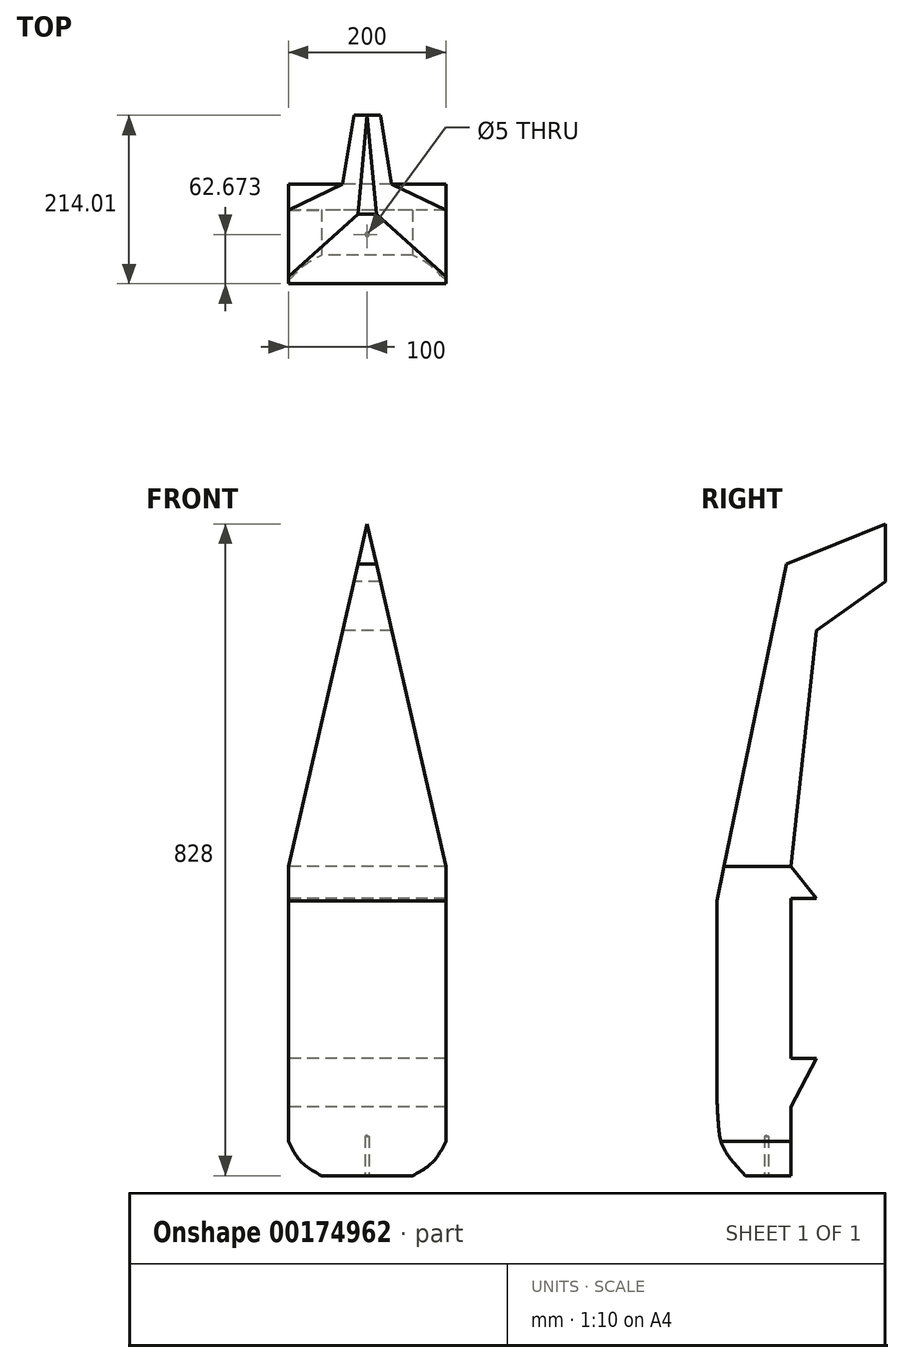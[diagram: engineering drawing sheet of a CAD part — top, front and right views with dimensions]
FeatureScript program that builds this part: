
annotation { "Feature Type Name" : "Feature", "Feature Type Description" : "" }
export const myFeature = defineFeature(function(context is Context, id is Id, definition is map)
    precondition{}
    {
        {
            var Q0;
            Q0=qCreatedBy(makeId("Top.planeOp"),FACE);
            var sketch = newSketch(context, id + "F0", { "sketchPlane" : qUnion([Q0])});
            skLineSegment(sketch, "E0.bottom", {"start": v(-100, 136) * mm, "end": v(100, 136) * mm});
            skLineSegment(sketch, "E0.top", {"start": v(-100, -136) * mm, "end": v(100, -136) * mm});
            skLineSegment(sketch, "E0.left", {"start": v(100, 136) * mm, "end": v(100, -136) * mm});
            skLineSegment(sketch, "E0.right", {"start": v(-100, 136) * mm, "end": v(-100, -136) * mm});
            skSolve(sketch);
        }
        {
            var Q0;
            Q0 = qSketchRegion(id + "F0", true);
            extrude(context, id + "F1", {"entities" : qUnion([Q0]), "endBound" : BoundingType.SYMMETRIC, "depth" : 828 * mm});
        }
        {
            var Q0;
            Q0=makeQuery(id+"F1.opExtrude","SWEPT_FACE",FACE,{"disambiguationData":[OSD([sQuery(id+"F0.wireOp",EDGE,"E0.right")])]});
            var sketch = newSketch(context, id + "F2", { "sketchPlane" : qUnion([Q0])});
            skLineSegment(sketch, "E1", {"start": v(-136, 414) * mm, "end": v(-136, 340.75) * mm});
            skLineSegment(sketch, "E2", {"start": v(-136, 340.75) * mm, "end": v(-48.64, 278.29) * mm});
            skLineSegment(sketch, "E3", {"start": v(-48.64, 278.29) * mm, "end": v(-15.68, -21.04) * mm});
            skLineSegment(sketch, "E4", {"start": v(-15.68, -21.04) * mm, "end": v(-48.64, -61.76) * mm});
            skLineSegment(sketch, "E5", {"start": v(-48.64, -61.76) * mm, "end": v(-15.68, -61.76) * mm});
            skLineSegment(sketch, "E6", {"start": v(-15.68, -61.76) * mm, "end": v(-15.68, -264.75) * mm});
            skLineSegment(sketch, "E7", {"start": v(-15.68, -264.75) * mm, "end": v(-48.64, -264.75) * mm});
            skLineSegment(sketch, "E8", {"start": v(-48.64, -264.75) * mm, "end": v(-15.68, -326.7) * mm});
            skPoint(sketch, "E8.endSnap0", {"position": v(-15.68, -163.26) * mm});
            skLineSegment(sketch, "E9", {"start": v(-15.68, -326.7) * mm, "end": v(-15.68, -414) * mm});
            skLineSegment(sketch, "E10", {"start": v(-15.68, -414) * mm, "end": v(41.58, -414) * mm});
            skFitSpline(sketch, "E11", {"points": [v(41.58, -414) * mm, v(69.34, -379.26) * mm, v(76.28, -348.03) * mm, v(78.01, -301.19) * mm], "startDerivative": vector(94.66, 99.8) * mm, "endDerivative": vector(0, 138.12) * mm});
            skLineSegment(sketch, "E12", {"start": v(78.01, -301.19) * mm, "end": v(78.01, -65.23) * mm});
            skLineSegment(sketch, "E13", {"start": v(78.01, -65.23) * mm, "end": v(-10.47, 363.3) * mm});
            skLineSegment(sketch, "E14", {"start": v(-10.47, 363.3) * mm, "end": v(-136, 414) * mm});
            skLineSegment(sketch, "E15.0", {"start": v(-136, 414) * mm, "end": v(-136, -414) * mm});
            skLineSegment(sketch, "E16.0", {"start": v(136, 414) * mm, "end": v(136, -414) * mm});
            skLineSegment(sketch, "E17.0", {"start": v(-136, 414) * mm, "end": v(136, 414) * mm});
            skLineSegment(sketch, "E18.0", {"start": v(-136, -414) * mm, "end": v(136, -414) * mm});
            skSolve(sketch);
        }
        {
            var Q0;
            {var subQ0=sQuery(id+"F2.wireOp",EDGE,"E2");Q0=makeQuery(id+"F2.imprint","IMPRINT",FACE,{"disambiguationData":[TD([[makeQuery(id+"F2.imprint","IMPRINT",EDGE,{"derivedFrom":subQ0}),-1.0]])]});}
            var Q1;
            {var subQ0=sQuery(id+"F2.wireOp",EDGE,"E11");Q1=makeQuery(id+"F2.imprint","IMPRINT",FACE,{"disambiguationData":[TD([[makeQuery(id+"F2.imprint","IMPRINT",EDGE,{"derivedFrom":subQ0}),-1.0]])]});}
            extrude(context, id + "F3", {"entities" : qUnion([Q0, Q1]), "operationType" : NewBodyOperationType.REMOVE, "endBound" : BoundingType.THROUGH_ALL, "oppositeDirection" : true, "depth" : 25 * mm});
        }
        {
            var Q0;
            Q0=makeQuery(id+"F3.boolean.opBoolean","COPY",FACE,{"derivedFrom":makeQuery(id+"F3.opExtrude","SWEPT_FACE",FACE,{"disambiguationData":[OSD([sQuery(id+"F2.wireOp",EDGE,"E12")])]})});
            var sketch = newSketch(context, id + "F4", { "sketchPlane" : qUnion([Q0])});
            skPoint(sketch, "E19.0", {"position": v(0, 414) * mm});
            skPoint(sketch, "E20.0", {"position": v(100, -21.04) * mm});
            skPoint(sketch, "E21.0", {"position": v(-100, -21.04) * mm});
            skPoint(sketch, "E22.0", {"position": v(100, -326.7) * mm});
            skPoint(sketch, "E23.0", {"position": v(100, -370.35) * mm});
            skPoint(sketch, "E24.0", {"position": v(100, -414) * mm});
            skLineSegment(sketch, "E25.0", {"start": v(100, -414) * mm, "end": v(-100, -414) * mm});
            skLineSegment(sketch, "E26.0.1", {"start": v(-100, -414) * mm, "end": v(-100, -326.7) * mm});
            skLineSegment(sketch, "E26.0.2", {"start": v(-100, -326.7) * mm, "end": v(100, -326.7) * mm});
            skLineSegment(sketch, "E26.0.3", {"start": v(100, -326.7) * mm, "end": v(100, -414) * mm});
            skLineSegment(sketch, "E27", {"start": v(0, 414) * mm, "end": v(100, -21.04) * mm});
            skLineSegment(sketch, "E28", {"start": v(-100, -21.04) * mm, "end": v(0, 414) * mm});
            skLineSegment(sketch, "E29", {"start": v(-100, -21.04) * mm, "end": v(100, -21.04) * mm});
            skFitSpline(sketch, "E30", {"points": [v(100, -370.35) * mm, v(84.02, -396.08) * mm, v(57.93, -414) * mm], "startDerivative": vector(-27.55, -56.15) * mm, "endDerivative": vector(-56.5, -31.25) * mm});
            skFitSpline(sketch, "E31.MirrorCS", {"points": [v(-100, -370.35) * mm, v(-84.02, -396.08) * mm, v(-57.93, -414) * mm], "startDerivative": vector(27.55, -56.15) * mm, "endDerivative": vector(56.5, -31.25) * mm});
            skLineSegment(sketch, "E32.0", {"start": v(100, -21.04) * mm, "end": v(100, 278.29) * mm});
            skLineSegment(sketch, "E33.0", {"start": v(100, 278.29) * mm, "end": v(100, 340.75) * mm});
            skLineSegment(sketch, "E34.0", {"start": v(100, 414) * mm, "end": v(100, 340.75) * mm});
            skLineSegment(sketch, "E35.0", {"start": v(-100, 414) * mm, "end": v(100, 414) * mm});
            skLineSegment(sketch, "E36.0", {"start": v(-100, 414) * mm, "end": v(-100, 340.75) * mm});
            skLineSegment(sketch, "E37.0", {"start": v(-100, 340.75) * mm, "end": v(-100, 278.29) * mm});
            skLineSegment(sketch, "E38.0", {"start": v(-100, 278.29) * mm, "end": v(-100, -21.04) * mm});
            skSolve(sketch);
        }
        {
            var Q0;
            {var subQ2=sQuery(id+"F4.wireOp",EDGE,"E28");Q0=makeQuery(id+"F4.imprint","IMPRINT",FACE,{"disambiguationData":[TD([[makeQuery(id+"F4.imprint","IMPRINT",EDGE,{"derivedFrom":subQ2}),1.0]])]});}
            var Q1;
            {var subQ1=sQuery(id+"F4.wireOp",EDGE,"E27");Q1=makeQuery(id+"F4.imprint","IMPRINT",FACE,{"disambiguationData":[TD([[makeQuery(id+"F4.imprint","IMPRINT",EDGE,{"derivedFrom":subQ1}),1.0]])]});}
            var Q2;
            {var subQ0=sQuery(id+"F4.wireOp",EDGE,"E30");Q2=makeQuery(id+"F4.imprint","IMPRINT",FACE,{"disambiguationData":[TD([[makeQuery(id+"F4.imprint","IMPRINT",EDGE,{"derivedFrom":subQ0}),1.0]])]});}
            var Q3;
            {var subQ0=sQuery(id+"F4.wireOp",EDGE,"E31.MirrorCS");Q3=makeQuery(id+"F4.imprint","IMPRINT",FACE,{"disambiguationData":[TD([[makeQuery(id+"F4.imprint","IMPRINT",EDGE,{"derivedFrom":subQ0}),-1.0]])]});}
            extrude(context, id + "F5", {"entities" : qUnion([Q0, Q1, Q2, Q3]), "operationType" : NewBodyOperationType.REMOVE, "endBound" : BoundingType.THROUGH_ALL, "oppositeDirection" : true, "depth" : 25 * mm});
        }
        {
            var Q0;
            Q0=makeQuery(id+"F1.opExtrude","CAP_FACE",FACE,{"disambiguationData":[OSD([sQuery(id+"F0.wireOp",EDGE,"E0.bottom"),sQuery(id+"F0.wireOp",EDGE,"E0.top"),sQuery(id+"F0.wireOp",EDGE,"E0.left"),sQuery(id+"F0.wireOp",EDGE,"E0.right")])],"isStart":true});
            var sketch = newSketch(context, id + "F6", { "sketchPlane" : qUnion([Q0])});
            skPoint(sketch, "E39", {"position": v(0, 15.34) * mm});
            skSolve(sketch);
        }
        {
            var Q0;
            Q0=sQuery(id+"F6.wireOp",VERTEX,"E39");
            var Q1;
            Q1=makeQuery(id+"F1.opExtrude","SWEPT_BODY",BODY,{"disambiguationData":[OSD([sQuery(id+"F0.wireOp",EDGE,"E0.bottom"),sQuery(id+"F0.wireOp",EDGE,"E0.top"),sQuery(id+"F0.wireOp",EDGE,"E0.left"),sQuery(id+"F0.wireOp",EDGE,"E0.right")])]});
            hole(context, id + "F7", {"style" : HoleStyle.SIMPLE, "endStyle" : HoleEndStyle.BLIND, "holeDiameter" : 5 * mm, "holeDepth" : 50 * mm, "locations" : qUnion([Q0]), "scope" : qUnion([Q1])});
        }
    });
